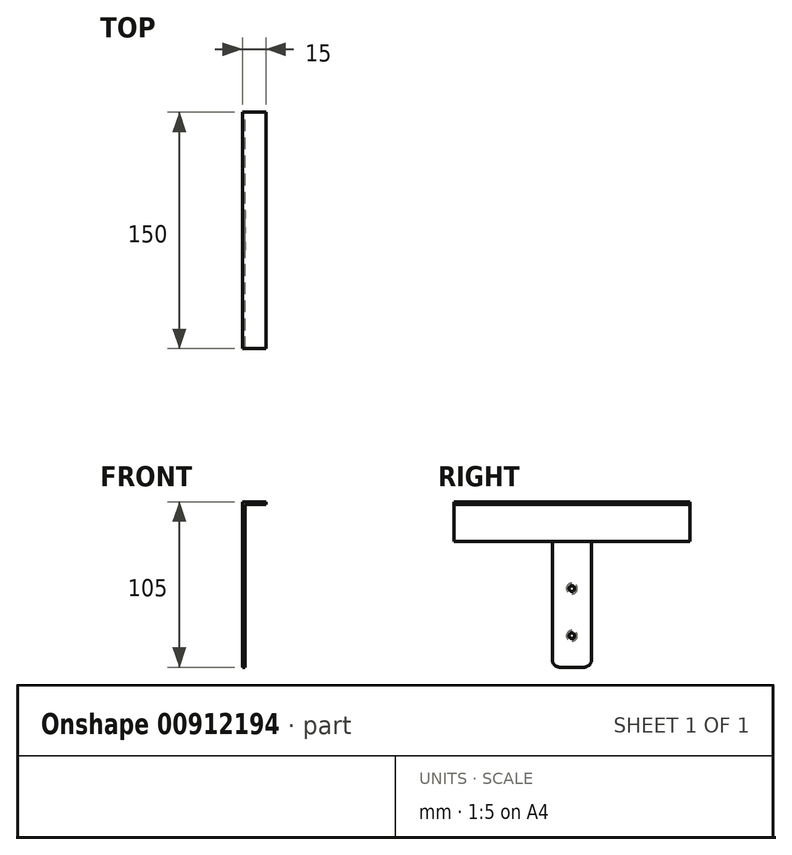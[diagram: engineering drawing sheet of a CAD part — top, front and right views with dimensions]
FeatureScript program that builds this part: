
annotation { "Feature Type Name" : "Feature", "Feature Type Description" : "" }
export const myFeature = defineFeature(function(context is Context, id is Id, definition is map)
    precondition{}
    {
        {
            var Q0;
            Q0=qCreatedBy(makeId("Front.planeOp"),FACE);
            var sketch = newSketch(context, id + "F0", { "sketchPlane" : qUnion([Q0])});
            skLineSegment(sketch, "E0", {"start": v(0, 0) * mm, "end": v(0, 25) * mm});
            skLineSegment(sketch, "E1", {"start": v(0, 25) * mm, "end": v(15, 25) * mm});
            skLineSegment(sketch, "E2", {"start": v(15, 25) * mm, "end": v(15, 23.41) * mm});
            skLineSegment(sketch, "E3", {"start": v(15, 23.41) * mm, "end": v(1.59, 23.41) * mm});
            skLineSegment(sketch, "E4", {"start": v(1.59, 23.41) * mm, "end": v(1.59, 0) * mm});
            skLineSegment(sketch, "E5", {"start": v(1.59, 0) * mm, "end": v(0, 0) * mm});
            skLineSegment(sketch, "E6", {"start": v(0, 0) * mm, "end": v(0, -80) * mm});
            skLineSegment(sketch, "E7", {"start": v(0, -80) * mm, "end": v(1.59, -80) * mm});
            skLineSegment(sketch, "E8", {"start": v(1.59, -80) * mm, "end": v(1.59, 0) * mm});
            skLineSegment(sketch, "E9.bottom", {"start": v(0, 25) * mm, "end": v(1.59, 25) * mm});
            skLineSegment(sketch, "E9.top", {"start": v(0, 75) * mm, "end": v(1.59, 75) * mm});
            skLineSegment(sketch, "E9.left", {"start": v(0, 25) * mm, "end": v(0, 75) * mm});
            skLineSegment(sketch, "E9.right", {"start": v(1.59, 25) * mm, "end": v(1.59, 75) * mm});
            skPoint(sketch, "E10", {"position": v(0, 50) * mm});
            skPoint(sketch, "E11", {"position": v(1.59, 12.3) * mm});
            skPoint(sketch, "E12", {"position": v(0, -30) * mm});
            skPoint(sketch, "E13", {"position": v(0, -60) * mm});
            skSolve(sketch);
        }
        {
            var Q0;
            Q0=qCreatedBy(makeId("Right.planeOp"),FACE);
            var sketch = newSketch(context, id + "F1", { "sketchPlane" : qUnion([Q0])});
            skPoint(sketch, "E14", {"position": v(0, 50) * mm});
            skPoint(sketch, "E15", {"position": v(0, -30) * mm});
            skPoint(sketch, "E16", {"position": v(0, -60) * mm});
            skPoint(sketch, "E17", {"position": v(0, 12.7) * mm});
            skSolve(sketch);
        }
        {
            var Q0;
            Q0=makeQuery(id+"F0.imprint","IMPRINT",FACE,{"disambiguationData":[TD([[makeQuery(id+"F0.imprint","IMPRINT",EDGE,{"derivedFrom":sQuery(id+"F0.wireOp",EDGE,"E6")}),1.0]])]});
            var Q1;
            Q1=makeQuery(id+"F0.imprint","IMPRINT",FACE,{"disambiguationData":[TD([[makeQuery(id+"F0.imprint","IMPRINT",EDGE,{"derivedFrom":sQuery(id+"F0.wireOp",EDGE,"E9.bottom")}),1.0]])]});
            extrude(context, id + "F2", {"entities" : qUnion([Q0, Q1]), "depth" : 25 * mm, "offsetDistance" : 25 * mm, "symmetric" : true});
        }
        {
            var Q0;
            Q0=makeQuery(id+"F0.imprint","IMPRINT",FACE,{"disambiguationData":[TD([[makeQuery(id+"F0.imprint","IMPRINT",EDGE,{"derivedFrom":sQuery(id+"F0.wireOp",EDGE,"E0")}),-1.0]])]});
            var Q1;
            Q1=sQuery(id+"F0.wireOp",EDGE,"E4");
            var Q2;
            Q2=sQuery(id+"F0.wireOp",EDGE,"E3");
            var Q3;
            Q3=sQuery(id+"F0.wireOp",EDGE,"E0");
            var Q4;
            Q4=sQuery(id+"F0.wireOp",EDGE,"E1");
            var Q5;
            Q5=sQuery(id+"F0.wireOp",EDGE,"E2");
            var Q6;
            Q6=sQuery(id+"F0.wireOp",EDGE,"E5");
            extrude(context, id + "F3", {"entities" : qUnion([Q0]), "surfaceEntities" : qUnion([Q1, Q2, Q3, Q4, Q5, Q6]), "depth" : 150 * mm, "offsetDistance" : 25 * mm, "symmetric" : true});
        }
        {
            var Q0;
            Q0=makeQuery(id+"F2.opExtrude","CAP_EDGE",EDGE,{"disambiguationData":[OSD([sQuery(id+"F0.wireOp",EDGE,"E9.top")])],"isStart":false});
            var Q1;
            Q1=makeQuery(id+"F2.opExtrude","CAP_EDGE",EDGE,{"disambiguationData":[OSD([sQuery(id+"F0.wireOp",EDGE,"E9.top")])],"isStart":true});
            var Q2;
            Q2=makeQuery(id+"F2.opExtrude","CAP_EDGE",EDGE,{"disambiguationData":[OSD([sQuery(id+"F0.wireOp",EDGE,"E7")])],"isStart":false});
            var Q3;
            Q3=makeQuery(id+"F2.opExtrude","CAP_EDGE",EDGE,{"disambiguationData":[OSD([sQuery(id+"F0.wireOp",EDGE,"E7")])],"isStart":true});
            fillet(context, id + "F4", {"entities" : qUnion([Q0, Q1, Q2, Q3]), "radius" : 5 * mm, "tangentPropagation" : true, "allowEdgeOverflow" : false});
        }
        {
            var Q0;
            Q0=sQuery(id+"F1.wireOp",VERTEX,"E14");
            var Q1;
            Q1=sQuery(id+"F1.wireOp",VERTEX,"E17");
            var Q2;
            Q2=sQuery(id+"F1.wireOp",VERTEX,"E15");
            var Q3;
            Q3=sQuery(id+"F1.wireOp",VERTEX,"E16");
            var Q4;
            Q4=makeQuery(id+"F2.opExtrude","SWEPT_BODY",BODY,{"disambiguationData":[OSD([sQuery(id+"F0.wireOp",EDGE,"E9.bottom"),sQuery(id+"F0.wireOp",EDGE,"E9.top"),sQuery(id+"F0.wireOp",EDGE,"E9.left"),sQuery(id+"F0.wireOp",EDGE,"E9.right")])]});
            var Q5;
            Q5=makeQuery(id+"F2.opExtrude","SWEPT_BODY",BODY,{"disambiguationData":[OSD([sQuery(id+"F0.wireOp",EDGE,"E6"),sQuery(id+"F0.wireOp",EDGE,"E7"),sQuery(id+"F0.wireOp",EDGE,"E8"),sQuery(id+"F0.wireOp",EDGE,"E5")])]});
            hole(context, id + "F5", {"style" : HoleStyle.C_SINK, "endStyle" : HoleEndStyle.THROUGH, "oppositeDirection" : true, "standardTappedOrClearance" : lookupTablePath({ "standard" : "ISO", "engagement" : "75%", "pitch" : "0.5 mm", "size" : "M3", "type" : "Tapped" }), "standardBlindInLast" : lookupTablePath({ "standard" : "ISO", "fit" : "Normal", "engagement" : "75%", "pitch" : "0.5 mm", "size" : "M3", "type" : "Clearance & tapped" }), "holeDiameter" : 2.5 * mm, "cSinkDiameter" : 6.72 * mm, "cSinkAngle" : 90 * degree, "majorDiameter" : 3 * mm, "showTappedDepth" : true, "isTappedThrough" : true, "tappedDepth" : 12 * mm, "tapClearance" : 3, "locations" : qUnion([Q0, Q1, Q2, Q3]), "scope" : qUnion([Q4, Q5]), "startStyle" : HoleStartStyle.PART});
        }
    });
